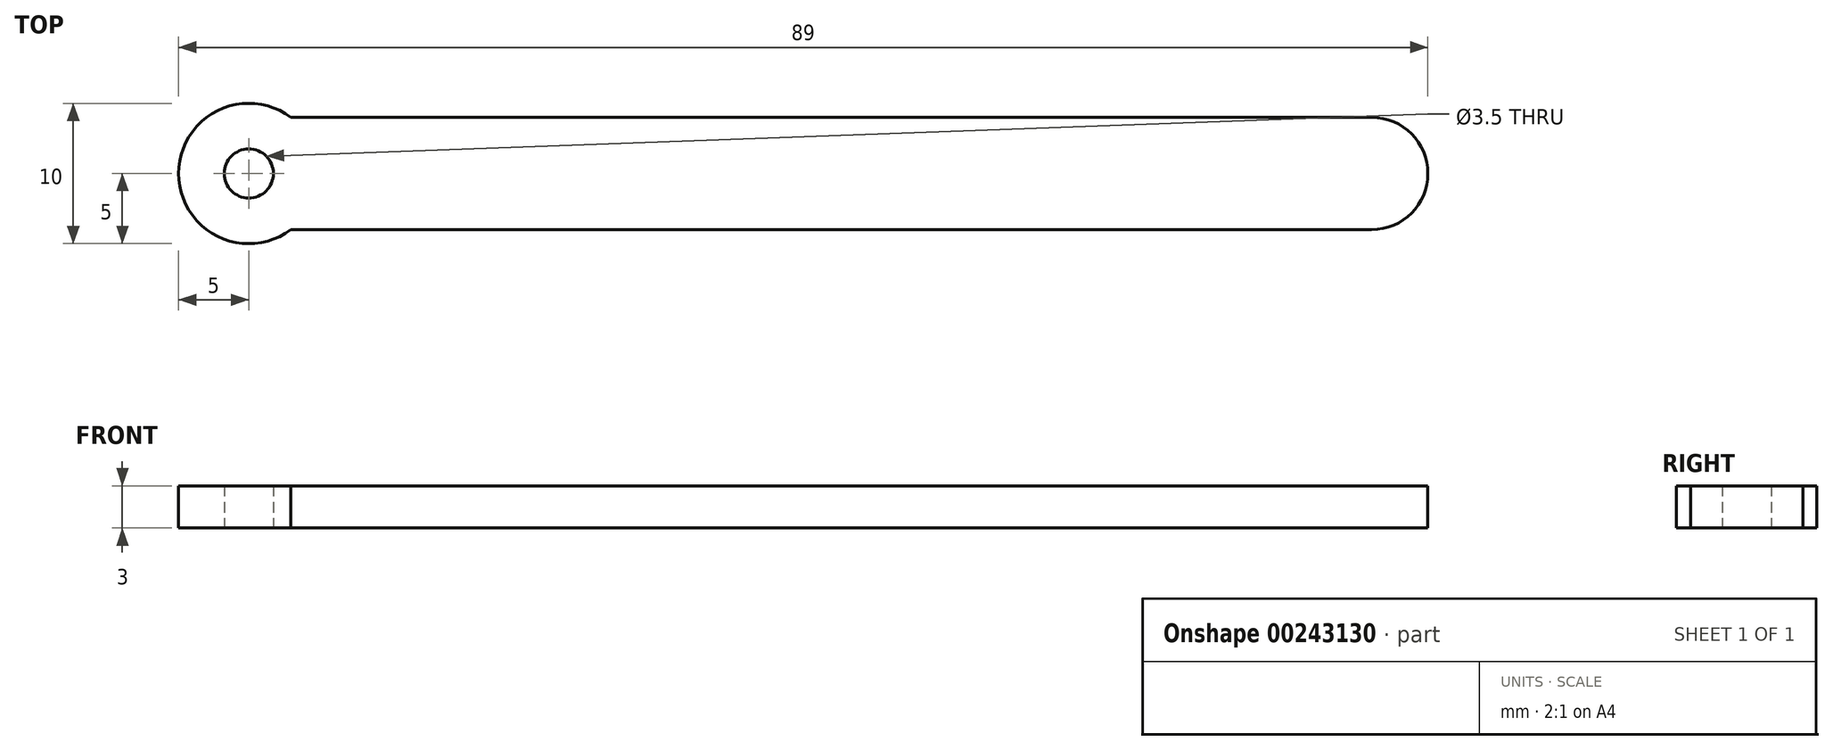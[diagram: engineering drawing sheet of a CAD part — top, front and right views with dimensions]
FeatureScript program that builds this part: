
annotation { "Feature Type Name" : "Feature", "Feature Type Description" : "" }
export const myFeature = defineFeature(function(context is Context, id is Id, definition is map)
    precondition{}
    {
        {
            var Q0;
            Q0=qCreatedBy(makeId("Top.planeOp"),FACE);
            var sketch = newSketch(context, id + "F0", { "sketchPlane" : qUnion([Q0])});
            skCircle(sketch, "E0", {"center": v(0, 0) * mm, "radius": 1.75 * mm});
            skArc(sketch, "E1", {"start": v(3, 4) * mm, "mid": v(-5, 0) * mm, "end": v(3, -4) * mm});
            skLineSegment(sketch, "E2.0", {"start": v(3, -4) * mm, "end": v(80, -4) * mm});
            skLineSegment(sketch, "E3.0", {"start": v(3, 4) * mm, "end": v(80, 4) * mm});
            skCircle(sketch, "E4", {"center": v(80, 0) * mm, "radius": 4 * mm});
            skSolve(sketch);
        }
        {
            var Q0;
            Q0 = qSketchRegion(id + "F0", true);
            extrude(context, id + "F1", {"entities" : qUnion([Q0]), "depth" : 3 * mm});
        }
    });
